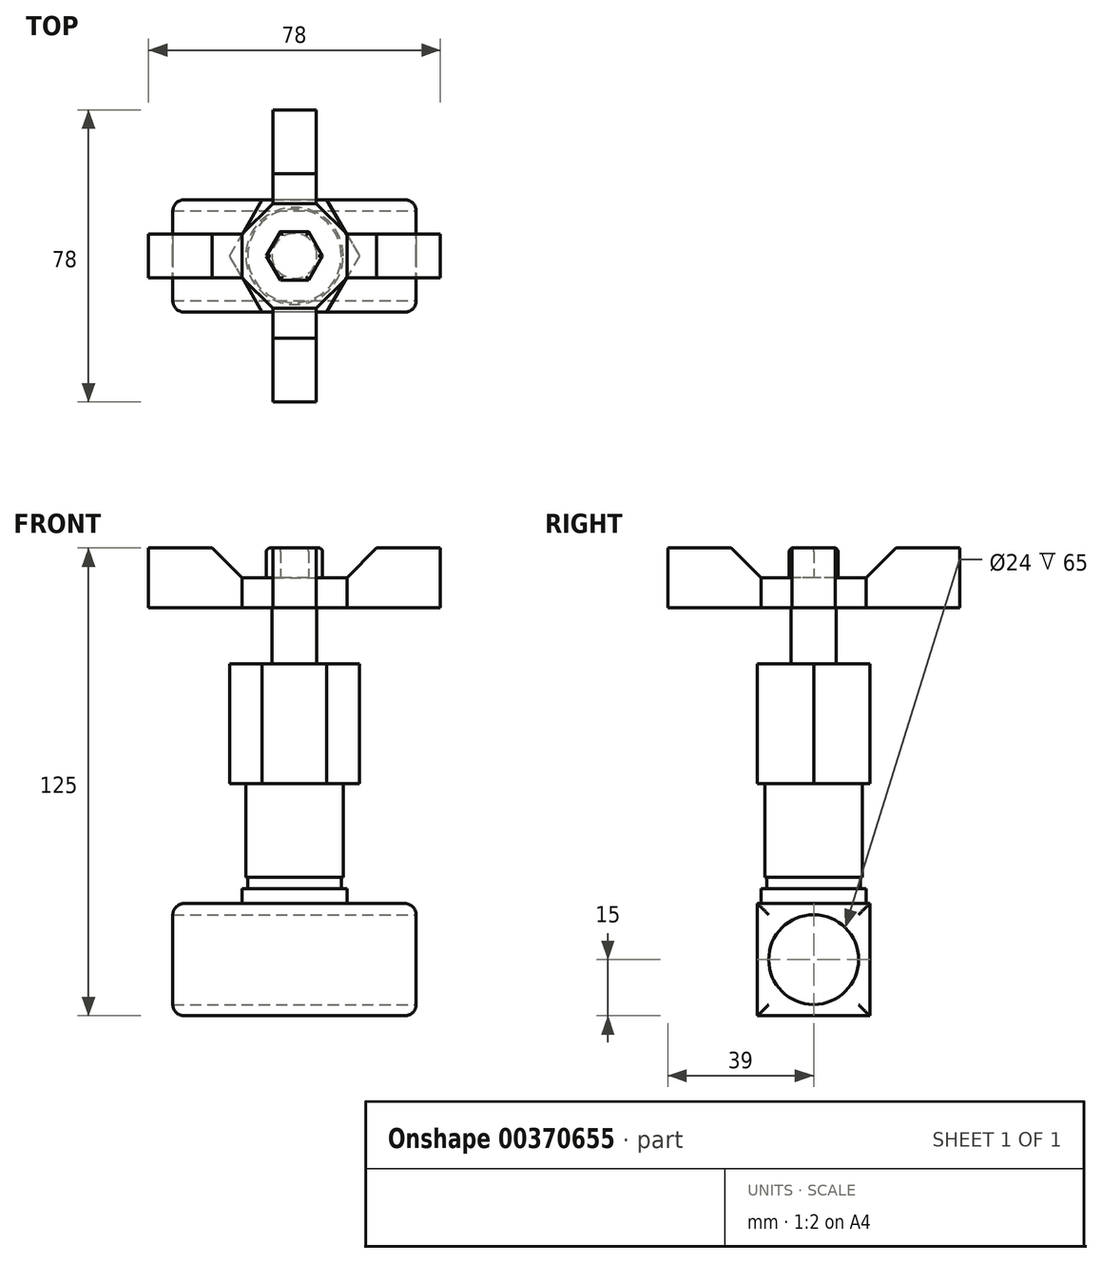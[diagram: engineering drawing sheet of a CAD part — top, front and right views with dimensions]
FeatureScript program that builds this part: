
annotation { "Feature Type Name" : "Feature", "Feature Type Description" : "" }
export const myFeature = defineFeature(function(context is Context, id is Id, definition is map)
    precondition{}
    {
        {
            var Q0;
            Q0=qCreatedBy(makeId("Top.planeOp"),FACE);
            var sketch = newSketch(context, id + "F0", { "sketchPlane" : qUnion([Q0])});
            skLineSegment(sketch, "E0.bottom", {"start": v(32.5, 15) * mm, "end": v(-32.5, 15) * mm});
            skLineSegment(sketch, "E0.top", {"start": v(32.5, -15) * mm, "end": v(-32.5, -15) * mm});
            skLineSegment(sketch, "E0.left", {"start": v(32.5, 15) * mm, "end": v(32.5, -15) * mm});
            skLineSegment(sketch, "E0.right", {"start": v(-32.5, 15) * mm, "end": v(-32.5, -15) * mm});
            skPoint(sketch, "E0.middle", {"position": v(0, 0) * mm});
            skSolve(sketch);
        }
        {
            var Q0;
            Q0=makeQuery(id+"F0.imprint","IMPRINT",FACE,{"disambiguationData":[TD([[makeQuery(id+"F0.imprint","IMPRINT",EDGE,{"derivedFrom":sQuery(id+"F0.wireOp",EDGE,"E0.bottom")}),1.0]])]});
            extrude(context, id + "F1", {"entities" : qUnion([Q0]), "depth" : 30 * mm});
        }
        {
            var Q0;
            Q0=makeQuery(id+"F1.opExtrude","SWEPT_FACE",FACE,{"disambiguationData":[OSD([sQuery(id+"F0.wireOp",EDGE,"E0.left")])]});
            var sketch = newSketch(context, id + "F2", { "sketchPlane" : qUnion([Q0])});
            skCircle(sketch, "E1", {"center": v(0, 15) * mm, "radius": 12 * mm});
            skSolve(sketch);
        }
        {
            var Q0;
            Q0=makeQuery(id+"F2.imprint","IMPRINT",FACE,{"disambiguationData":[TD([[makeQuery(id+"F2.imprint","IMPRINT",EDGE,{"derivedFrom":sQuery(id+"F2.wireOp",EDGE,"E1")}),1.0]])]});
            extrude(context, id + "F3", {"entities" : qUnion([Q0]), "operationType" : NewBodyOperationType.REMOVE, "oppositeDirection" : true, "depth" : 65 * mm});
        }
        {
            var Q0;
            Q0=makeQuery(id+"F1.opExtrude","CAP_FACE",FACE,{"disambiguationData":[OSD([sQuery(id+"F0.wireOp",EDGE,"E0.bottom"),sQuery(id+"F0.wireOp",EDGE,"E0.top"),sQuery(id+"F0.wireOp",EDGE,"E0.left"),sQuery(id+"F0.wireOp",EDGE,"E0.right")])],"isStart":false});
            var sketch = newSketch(context, id + "F4", { "sketchPlane" : qUnion([Q0])});
            skCircle(sketch, "E2", {"center": v(0, 0) * mm, "radius": 14 * mm});
            skSolve(sketch);
        }
        {
            var Q0;
            Q0=makeQuery(id+"F4.imprint","IMPRINT",FACE,{"disambiguationData":[TD([[makeQuery(id+"F4.imprint","IMPRINT",EDGE,{"derivedFrom":sQuery(id+"F4.wireOp",EDGE,"E2")}),1.0]])]});
            extrude(context, id + "F5", {"entities" : qUnion([Q0]), "operationType" : NewBodyOperationType.ADD, "depth" : 4 * mm});
        }
        {
            var Q0;
            Q0=makeQuery(id+"F5.opExtrude","CAP_FACE",FACE,{"disambiguationData":[OSD([sQuery(id+"F4.wireOp",EDGE,"E2")])],"isStart":false});
            var sketch = newSketch(context, id + "F6", { "sketchPlane" : qUnion([Q0])});
            skCircle(sketch, "E3", {"center": v(0, 0) * mm, "radius": 12.5 * mm});
            skSolve(sketch);
        }
        {
            var Q0;
            Q0=makeQuery(id+"F6.imprint","IMPRINT",FACE,{"disambiguationData":[TD([[makeQuery(id+"F6.imprint","IMPRINT",EDGE,{"derivedFrom":sQuery(id+"F6.wireOp",EDGE,"E3")}),1.0]])]});
            extrude(context, id + "F7", {"entities" : qUnion([Q0]), "operationType" : NewBodyOperationType.ADD, "depth" : 3 * mm});
        }
        {
            var Q0;
            Q0=makeQuery(id+"F7.opExtrude","CAP_FACE",FACE,{"disambiguationData":[OSD([sQuery(id+"F6.wireOp",EDGE,"E3")])],"isStart":false});
            var sketch = newSketch(context, id + "F8", { "sketchPlane" : qUnion([Q0])});
            skCircle(sketch, "E4", {"center": v(0, 0) * mm, "radius": 13 * mm});
            skSolve(sketch);
        }
        {
            var Q0;
            Q0=makeQuery(id+"F8.imprint","IMPRINT",FACE,{"disambiguationData":[TD([[makeQuery(id+"F8.imprint","IMPRINT",EDGE,{"derivedFrom":sQuery(id+"F8.wireOp",EDGE,"E4")}),1.0]])]});
            var Q1;
            Q1=makeQuery(id+"F8.imprint","IMPRINT",FACE,{"disambiguationData":[TD([[makeQuery(id+"F8.imprint","IMPRINT",EDGE,{"derivedFrom":makeQuery(id+"F7.opExtrude","CAP_EDGE",EDGE,{"disambiguationData":[OSD([sQuery(id+"F6.wireOp",EDGE,"E3")])],"isStart":false})}),1.0]])]});
            extrude(context, id + "F9", {"entities" : qUnion([Q0, Q1]), "operationType" : NewBodyOperationType.ADD, "depth" : 25 * mm});
        }
        {
            var Q0;
            Q0=makeQuery(id+"F9.opExtrude","CAP_FACE",FACE,{"disambiguationData":[OSD([sQuery(id+"F8.wireOp",EDGE,"E4")])],"isStart":false});
            var sketch = newSketch(context, id + "F10", { "sketchPlane" : qUnion([Q0])});
            skCircle(sketch, "E5.cCircle", {"center": v(0, 0) * mm, "radius": 15 * mm, "construction": true});
            skLineSegment(sketch, "E5.0", {"start": v(8.66, 15) * mm, "end": v(17.32, 0) * mm});
            skLineSegment(sketch, "E5.1", {"start": v(17.32, 0) * mm, "end": v(8.66, -15) * mm});
            skLineSegment(sketch, "E5.2", {"start": v(8.66, -15) * mm, "end": v(-8.66, -15) * mm});
            skLineSegment(sketch, "E5.3", {"start": v(-8.66, -15) * mm, "end": v(-17.32, 0) * mm});
            skLineSegment(sketch, "E5.4", {"start": v(-17.32, 0) * mm, "end": v(-8.66, 15) * mm});
            skLineSegment(sketch, "E5.5", {"start": v(-8.66, 15) * mm, "end": v(8.66, 15) * mm});
            skPoint(sketch, "E5.0.midPoint", {"position": v(13, 7.5) * mm});
            skSolve(sketch);
        }
        {
            var Q0;
            Q0=makeQuery(id+"F10.imprint","IMPRINT",FACE,{"disambiguationData":[TD([[makeQuery(id+"F10.imprint","IMPRINT",EDGE,{"derivedFrom":makeQuery(id+"F9.opExtrude","CAP_EDGE",EDGE,{"disambiguationData":[OSD([sQuery(id+"F8.wireOp",EDGE,"E4")])],"isStart":false})}),1.0]])]});
            var Q1;
            Q1=makeQuery(id+"F10.imprint","IMPRINT",FACE,{"disambiguationData":[TD([[makeQuery(id+"F10.imprint","IMPRINT",EDGE,{"derivedFrom":sQuery(id+"F10.wireOp",EDGE,"E5.0")}),-1.0]])]});
            extrude(context, id + "F11", {"entities" : qUnion([Q0, Q1]), "operationType" : NewBodyOperationType.ADD, "depth" : 32 * mm});
        }
        {
            var Q0;
            Q0=makeQuery(id+"F11.opExtrude","CAP_FACE",FACE,{"disambiguationData":[OSD([sQuery(id+"F10.wireOp",EDGE,"E5.0"),sQuery(id+"F10.wireOp",EDGE,"E5.1"),sQuery(id+"F10.wireOp",EDGE,"E5.2"),sQuery(id+"F10.wireOp",EDGE,"E5.3"),sQuery(id+"F10.wireOp",EDGE,"E5.4"),sQuery(id+"F10.wireOp",EDGE,"E5.5")])],"isStart":false});
            var sketch = newSketch(context, id + "F12", { "sketchPlane" : qUnion([Q0])});
            skCircle(sketch, "E6", {"center": v(0, 0) * mm, "radius": 6 * mm});
            skSolve(sketch);
        }
        {
            var Q0;
            Q0=makeQuery(id+"F12.imprint","IMPRINT",FACE,{"disambiguationData":[TD([[makeQuery(id+"F12.imprint","IMPRINT",EDGE,{"derivedFrom":sQuery(id+"F12.wireOp",EDGE,"E6")}),1.0]])]});
            extrude(context, id + "F13", {"entities" : qUnion([Q0]), "operationType" : NewBodyOperationType.ADD, "depth" : 15 * mm});
        }
        {
            var Q0;
            Q0=makeQuery(id+"F13.opExtrude","CAP_FACE",FACE,{"disambiguationData":[OSD([sQuery(id+"F12.wireOp",EDGE,"E6")])],"isStart":false});
            var sketch = newSketch(context, id + "F14", { "sketchPlane" : qUnion([Q0])});
            skCircle(sketch, "E7.cCircle", {"center": v(0, 0) * mm, "radius": 14 * mm, "construction": true});
            skLineSegment(sketch, "E7.0", {"start": v(14, -5.8) * mm, "end": v(5.8, -14) * mm});
            skLineSegment(sketch, "E7.1", {"start": v(5.8, -14) * mm, "end": v(-5.8, -14) * mm});
            skLineSegment(sketch, "E7.2", {"start": v(-5.8, -14) * mm, "end": v(-14, -5.8) * mm});
            skLineSegment(sketch, "E7.3", {"start": v(-14, -5.8) * mm, "end": v(-14, 5.8) * mm});
            skLineSegment(sketch, "E7.4", {"start": v(-14, 5.8) * mm, "end": v(-5.8, 14) * mm});
            skLineSegment(sketch, "E7.5", {"start": v(-5.8, 14) * mm, "end": v(5.8, 14) * mm});
            skLineSegment(sketch, "E7.6", {"start": v(5.8, 14) * mm, "end": v(14, 5.8) * mm});
            skLineSegment(sketch, "E7.7", {"start": v(14, 5.8) * mm, "end": v(14, -5.8) * mm});
            skPoint(sketch, "E7.0.midPoint", {"position": v(9.9, -9.9) * mm});
            skSolve(sketch);
        }
        {
            var Q0;
            Q0=makeQuery(id+"F14.imprint","IMPRINT",FACE,{"disambiguationData":[TD([[makeQuery(id+"F14.imprint","IMPRINT",EDGE,{"derivedFrom":makeQuery(id+"F13.opExtrude","CAP_EDGE",EDGE,{"disambiguationData":[OSD([sQuery(id+"F12.wireOp",EDGE,"E6")])],"isStart":false})}),1.0]])]});
            var Q1;
            Q1=makeQuery(id+"F14.imprint","IMPRINT",FACE,{"disambiguationData":[TD([[makeQuery(id+"F14.imprint","IMPRINT",EDGE,{"derivedFrom":sQuery(id+"F14.wireOp",EDGE,"E7.0")}),-1.0]])]});
            extrude(context, id + "F15", {"entities" : qUnion([Q0, Q1]), "operationType" : NewBodyOperationType.ADD, "depth" : 8 * mm});
        }
        {
            var Q0;
            Q0=makeQuery(id+"F15.opExtrude","SWEPT_FACE",FACE,{"disambiguationData":[OSD([sQuery(id+"F14.wireOp",EDGE,"E7.7")])]});
            extrude(context, id + "F16", {"entities" : qUnion([Q0]), "operationType" : NewBodyOperationType.ADD, "depth" : 25 * mm});
        }
        {
            var Q0;
            Q0=makeQuery(id+"F15.opExtrude","SWEPT_FACE",FACE,{"disambiguationData":[OSD([sQuery(id+"F14.wireOp",EDGE,"E7.1")])]});
            extrude(context, id + "F17", {"entities" : qUnion([Q0]), "operationType" : NewBodyOperationType.ADD, "depth" : 25 * mm});
        }
        {
            var Q0;
            Q0=makeQuery(id+"F15.opExtrude","SWEPT_FACE",FACE,{"disambiguationData":[OSD([sQuery(id+"F14.wireOp",EDGE,"E7.3")])]});
            extrude(context, id + "F18", {"entities" : qUnion([Q0]), "operationType" : NewBodyOperationType.ADD, "depth" : 25 * mm});
        }
        {
            var Q0;
            Q0=makeQuery(id+"F15.opExtrude","SWEPT_FACE",FACE,{"disambiguationData":[OSD([sQuery(id+"F14.wireOp",EDGE,"E7.5")])]});
            extrude(context, id + "F19", {"entities" : qUnion([Q0]), "operationType" : NewBodyOperationType.ADD, "depth" : 25 * mm});
        }
        {
            var Q0;
            {var subQ0=sQuery(id+"F14.wireOp",EDGE,"E7.5");var subQ1=sQuery(id+"F14.wireOp",EDGE,"E7.3");var subQ2=sQuery(id+"F14.wireOp",EDGE,"E7.1");var subQ3=sQuery(id+"F14.wireOp",EDGE,"E7.7");Q0=makeQuery(id+"F19.boolean.opBoolean","MERGE",FACE,{"derivedFrom":[makeQuery(id+"F18.boolean.opBoolean","MERGE",FACE,{"derivedFrom":[makeQuery(id+"F17.boolean.opBoolean","MERGE",FACE,{"derivedFrom":[makeQuery(id+"F16.boolean.opBoolean","MERGE",FACE,{"derivedFrom":[makeQuery(id+"F15.opExtrude","CAP_FACE",FACE,{"disambiguationData":[OSD([sQuery(id+"F14.wireOp",EDGE,"E7.0"),subQ2,sQuery(id+"F14.wireOp",EDGE,"E7.2"),subQ1,sQuery(id+"F14.wireOp",EDGE,"E7.4"),subQ0,sQuery(id+"F14.wireOp",EDGE,"E7.6"),subQ3])],"isStart":false}),makeQuery(id+"F16.opExtrude","SWEPT_FACE",FACE,{"disambiguationData":[OSD([subQ3]),TDD([makeQuery(id+"F15.opExtrude","CAP_EDGE",EDGE,{"disambiguationData":[OSD([subQ3])],"isStart":false})])]})]}),makeQuery(id+"F17.opExtrude","SWEPT_FACE",FACE,{"disambiguationData":[OSD([subQ2]),TDD([makeQuery(id+"F15.opExtrude","CAP_EDGE",EDGE,{"disambiguationData":[OSD([subQ2])],"isStart":false})])]})]}),makeQuery(id+"F18.opExtrude","SWEPT_FACE",FACE,{"disambiguationData":[OSD([subQ1]),TDD([makeQuery(id+"F15.opExtrude","CAP_EDGE",EDGE,{"disambiguationData":[OSD([subQ1])],"isStart":false})])]})]}),makeQuery(id+"F19.opExtrude","SWEPT_FACE",FACE,{"disambiguationData":[OSD([subQ0]),TDD([makeQuery(id+"F15.opExtrude","CAP_EDGE",EDGE,{"disambiguationData":[OSD([subQ0])],"isStart":false})])]})]});}
            var sketch = newSketch(context, id + "F20", { "sketchPlane" : qUnion([Q0])});
            skLineSegment(sketch, "E8.bottom", {"start": v(39, 5.8) * mm, "end": v(14, 5.8) * mm});
            skLineSegment(sketch, "E8.top", {"start": v(39, -5.8) * mm, "end": v(14, -5.8) * mm});
            skLineSegment(sketch, "E8.left", {"start": v(39, 5.8) * mm, "end": v(39, -5.8) * mm});
            skLineSegment(sketch, "E8.right", {"start": v(14, 5.8) * mm, "end": v(14, -5.8) * mm});
            skLineSegment(sketch, "E9.bottom", {"start": v(-5.8, 39) * mm, "end": v(5.8, 39) * mm});
            skLineSegment(sketch, "E9.top", {"start": v(-5.8, 14) * mm, "end": v(5.8, 14) * mm});
            skLineSegment(sketch, "E9.left", {"start": v(-5.8, 39) * mm, "end": v(-5.8, 14) * mm});
            skLineSegment(sketch, "E9.right", {"start": v(5.8, 39) * mm, "end": v(5.8, 14) * mm});
            skLineSegment(sketch, "E10.bottom", {"start": v(-39, -5.8) * mm, "end": v(-14, -5.8) * mm});
            skLineSegment(sketch, "E10.top", {"start": v(-39, 5.8) * mm, "end": v(-14, 5.8) * mm});
            skLineSegment(sketch, "E10.left", {"start": v(-39, -5.8) * mm, "end": v(-39, 5.8) * mm});
            skLineSegment(sketch, "E10.right", {"start": v(-14, -5.8) * mm, "end": v(-14, 5.8) * mm});
            skLineSegment(sketch, "E11.bottom", {"start": v(-5.8, -39) * mm, "end": v(5.8, -39) * mm});
            skLineSegment(sketch, "E11.top", {"start": v(-5.8, -14) * mm, "end": v(5.8, -14) * mm});
            skLineSegment(sketch, "E11.left", {"start": v(-5.8, -39) * mm, "end": v(-5.8, -14) * mm});
            skLineSegment(sketch, "E11.right", {"start": v(5.8, -39) * mm, "end": v(5.8, -14) * mm});
            skSolve(sketch);
        }
        {
            var Q0;
            {var subQ0=sQuery(id+"F20.wireOp",EDGE,"E9.top");Q0=makeQuery(id+"F20.imprint","IMPRINT",FACE,{"disambiguationData":[TD([[makeQuery(id+"F20.imprint","IMPRINT",EDGE,{"derivedFrom":subQ0}),1.0]])]});}
            var Q1;
            {var subQ0=sQuery(id+"F20.wireOp",EDGE,"E10.bottom");Q1=makeQuery(id+"F20.imprint","IMPRINT",FACE,{"disambiguationData":[TD([[makeQuery(id+"F20.imprint","IMPRINT",EDGE,{"derivedFrom":subQ0}),1.0]])]});}
            var Q2;
            {var subQ1=sQuery(id+"F14.wireOp",EDGE,"E7.1");var subQ2=sQuery(id+"F14.wireOp",EDGE,"E7.2");var subQ3=makeQuery(id+"F17.opExtrude","SWEPT_EDGE",EDGE,{"disambiguationData":[OSD([subQ1,subQ2]),TDD([makeQuery(id+"F15.opExtrude","CAP_VERTEX",VERTEX,{"disambiguationData":[OSD([subQ1,subQ2])],"isStart":false})])]});var subQ8=sQuery(id+"F20.wireOp",EDGE,"E11.top");var subQ10=makeQuery(id+"F20.imprint","INTERSECT",VERTEX,{"derivedFrom":[subQ3,subQ8]});Q2=makeQuery(id+"F20.imprint","IMPRINT",FACE,{"disambiguationData":[TD([[makeQuery(id+"F20.imprint","IMPRINT",EDGE,{"disambiguationData":[TD([[subQ10,-1.0]])],"derivedFrom":subQ8}),-1.0]])]});}
            var Q3;
            {var subQ0=sQuery(id+"F20.wireOp",EDGE,"E8.bottom");Q3=makeQuery(id+"F20.imprint","IMPRINT",FACE,{"disambiguationData":[TD([[makeQuery(id+"F20.imprint","IMPRINT",EDGE,{"derivedFrom":subQ0}),1.0]])]});}
            extrude(context, id + "F21", {"entities" : qUnion([Q0, Q1, Q2, Q3]), "operationType" : NewBodyOperationType.ADD, "depth" : 8 * mm});
        }
        {
            var Q0;
            Q0=makeQuery(id+"F21.opExtrude","CAP_EDGE",EDGE,{"disambiguationData":[OSD([sQuery(id+"F20.wireOp",EDGE,"E10.right")])],"isStart":false});
            var Q1;
            Q1=makeQuery(id+"F21.opExtrude","CAP_EDGE",EDGE,{"disambiguationData":[OSD([sQuery(id+"F20.wireOp",EDGE,"E11.top")])],"isStart":false});
            var Q2;
            Q2=makeQuery(id+"F21.opExtrude","CAP_EDGE",EDGE,{"disambiguationData":[OSD([sQuery(id+"F20.wireOp",EDGE,"E8.right")])],"isStart":false});
            var Q3;
            Q3=makeQuery(id+"F21.opExtrude","CAP_EDGE",EDGE,{"disambiguationData":[OSD([sQuery(id+"F20.wireOp",EDGE,"E9.top")])],"isStart":false});
            chamfer(context, id + "F22", {"entities" : qUnion([Q0, Q1, Q2, Q3]), "width" : 8 * mm, "tangentPropagation" : true});
        }
        {
            var Q0;
            Q0=makeQuery(id+"F1.opExtrude","SWEPT_EDGE",EDGE,{"disambiguationData":[OSD([sQuery(id+"F0.wireOp",EDGE,"E0.top"),sQuery(id+"F0.wireOp",EDGE,"E0.left")])]});
            var Q1;
            Q1=makeQuery(id+"F1.opExtrude","CAP_EDGE",EDGE,{"disambiguationData":[OSD([sQuery(id+"F0.wireOp",EDGE,"E0.left")])],"isStart":false});
            var Q2;
            Q2=makeQuery(id+"F1.opExtrude","SWEPT_EDGE",EDGE,{"disambiguationData":[OSD([sQuery(id+"F0.wireOp",EDGE,"E0.bottom"),sQuery(id+"F0.wireOp",EDGE,"E0.left")])]});
            var Q3;
            Q3=makeQuery(id+"F1.opExtrude","CAP_EDGE",EDGE,{"disambiguationData":[OSD([sQuery(id+"F0.wireOp",EDGE,"E0.left")])],"isStart":true});
            fillet(context, id + "F23", {"entities" : qUnion([Q0, Q1, Q2, Q3]), "radius" : 3 * mm, "tangentPropagation" : true, "allowEdgeOverflow" : false});
        }
        {
            var Q0;
            Q0=makeQuery(id+"F1.opExtrude","CAP_EDGE",EDGE,{"disambiguationData":[OSD([sQuery(id+"F0.wireOp",EDGE,"E0.right")])],"isStart":false});
            var Q1;
            Q1=makeQuery(id+"F1.opExtrude","SWEPT_EDGE",EDGE,{"disambiguationData":[OSD([sQuery(id+"F0.wireOp",EDGE,"E0.bottom"),sQuery(id+"F0.wireOp",EDGE,"E0.right")])]});
            var Q2;
            Q2=makeQuery(id+"F1.opExtrude","SWEPT_EDGE",EDGE,{"disambiguationData":[OSD([sQuery(id+"F0.wireOp",EDGE,"E0.top"),sQuery(id+"F0.wireOp",EDGE,"E0.right")])]});
            var Q3;
            Q3=makeQuery(id+"F1.opExtrude","CAP_EDGE",EDGE,{"disambiguationData":[OSD([sQuery(id+"F0.wireOp",EDGE,"E0.right")])],"isStart":true});
            fillet(context, id + "F24", {"entities" : qUnion([Q0, Q1, Q2, Q3]), "radius" : 3 * mm, "tangentPropagation" : true, "allowEdgeOverflow" : false});
        }
        {
            var Q0;
            {var subQ0=sQuery(id+"F14.wireOp",EDGE,"E7.5");var subQ1=sQuery(id+"F14.wireOp",EDGE,"E7.4");var subQ2=sQuery(id+"F14.wireOp",EDGE,"E7.3");var subQ3=makeQuery(id+"F18.opExtrude","SWEPT_FACE",FACE,{"disambiguationData":[OSD([subQ2]),TDD([makeQuery(id+"F15.opExtrude","CAP_EDGE",EDGE,{"disambiguationData":[OSD([subQ2])],"isStart":false})])]});var subQ4=sQuery(id+"F14.wireOp",EDGE,"E7.1");var subQ5=makeQuery(id+"F17.opExtrude","SWEPT_FACE",FACE,{"disambiguationData":[OSD([subQ4]),TDD([makeQuery(id+"F15.opExtrude","CAP_EDGE",EDGE,{"disambiguationData":[OSD([subQ4])],"isStart":false})])]});var subQ6=sQuery(id+"F14.wireOp",EDGE,"E7.2");var subQ7=makeQuery(id+"F19.opExtrude","SWEPT_FACE",FACE,{"disambiguationData":[OSD([subQ0]),TDD([makeQuery(id+"F15.opExtrude","CAP_EDGE",EDGE,{"disambiguationData":[OSD([subQ0])],"isStart":false})])]});var subQ8=sQuery(id+"F14.wireOp",EDGE,"E7.7");var subQ9=makeQuery(id+"F16.opExtrude","SWEPT_FACE",FACE,{"disambiguationData":[OSD([subQ8]),TDD([makeQuery(id+"F15.opExtrude","CAP_EDGE",EDGE,{"disambiguationData":[OSD([subQ8])],"isStart":false})])]});var subQ10=sQuery(id+"F14.wireOp",EDGE,"E7.0");var subQ11=sQuery(id+"F14.wireOp",EDGE,"E7.6");var subQ12=makeQuery(id+"F15.opExtrude","CAP_FACE",FACE,{"disambiguationData":[OSD([subQ10,subQ4,subQ6,subQ2,subQ1,subQ0,subQ11,subQ8])],"isStart":false});Q0=makeQuery(id+"F21.boolean.opBoolean","SPLIT",FACE,{"disambiguationData":[TD([makeQuery(id+"F15.opExtrude","SWEPT_FACE",FACE,{"disambiguationData":[OSD([subQ10])]}),subQ12,makeQuery(id+"F15.opExtrude","SWEPT_FACE",FACE,{"disambiguationData":[OSD([subQ6])]}),makeQuery(id+"F15.opExtrude","SWEPT_FACE",FACE,{"disambiguationData":[OSD([subQ1])]}),makeQuery(id+"F15.opExtrude","SWEPT_FACE",FACE,{"disambiguationData":[OSD([subQ11])]}),makeQuery(id+"F16.opExtrude","SWEPT_FACE",FACE,{"disambiguationData":[OSD([subQ10,subQ8])]}),makeQuery(id+"F16.opExtrude","SWEPT_FACE",FACE,{"disambiguationData":[OSD([subQ11,subQ8])]}),subQ9,makeQuery(id+"F16.opExtrude","CAP_FACE",FACE,{"disambiguationData":[OSD([subQ8])],"isStart":false}),makeQuery(id+"F17.opExtrude","SWEPT_FACE",FACE,{"disambiguationData":[OSD([subQ10,subQ4])]}),makeQuery(id+"F17.opExtrude","SWEPT_FACE",FACE,{"disambiguationData":[OSD([subQ4,subQ6])]}),subQ5,makeQuery(id+"F18.opExtrude","SWEPT_FACE",FACE,{"disambiguationData":[OSD([subQ6,subQ2])]}),makeQuery(id+"F18.opExtrude","SWEPT_FACE",FACE,{"disambiguationData":[OSD([subQ2,subQ1])]}),subQ3,makeQuery(id+"F18.opExtrude","CAP_FACE",FACE,{"disambiguationData":[OSD([subQ2])],"isStart":false}),makeQuery(id+"F19.opExtrude","SWEPT_FACE",FACE,{"disambiguationData":[OSD([subQ1,subQ0])]}),makeQuery(id+"F19.opExtrude","SWEPT_FACE",FACE,{"disambiguationData":[OSD([subQ0,subQ11])]}),subQ7,makeQuery(id+"F19.opExtrude","CAP_FACE",FACE,{"disambiguationData":[OSD([subQ0])],"isStart":false}),makeQuery(id+"F21.opExtrude","SWEPT_FACE",FACE,{"disambiguationData":[OSD([sQuery(id+"F20.wireOp",EDGE,"E8.bottom")])]}),makeQuery(id+"F21.opExtrude","SWEPT_FACE",FACE,{"disambiguationData":[OSD([sQuery(id+"F20.wireOp",EDGE,"E8.top")])]}),makeQuery(id+"F21.opExtrude","SWEPT_FACE",FACE,{"disambiguationData":[OSD([sQuery(id+"F20.wireOp",EDGE,"E8.right")])]}),makeQuery(id+"F21.opExtrude","SWEPT_FACE",FACE,{"disambiguationData":[OSD([sQuery(id+"F20.wireOp",EDGE,"E9.top")])]}),makeQuery(id+"F21.opExtrude","SWEPT_FACE",FACE,{"disambiguationData":[OSD([sQuery(id+"F20.wireOp",EDGE,"E9.left")])]}),makeQuery(id+"F21.opExtrude","SWEPT_FACE",FACE,{"disambiguationData":[OSD([sQuery(id+"F20.wireOp",EDGE,"E9.right")])]}),makeQuery(id+"F21.opExtrude","SWEPT_FACE",FACE,{"disambiguationData":[OSD([sQuery(id+"F20.wireOp",EDGE,"E10.bottom")])]}),makeQuery(id+"F21.opExtrude","SWEPT_FACE",FACE,{"disambiguationData":[OSD([sQuery(id+"F20.wireOp",EDGE,"E10.top")])]}),makeQuery(id+"F21.opExtrude","SWEPT_FACE",FACE,{"disambiguationData":[OSD([sQuery(id+"F20.wireOp",EDGE,"E10.right")])]}),makeQuery(id+"F21.opExtrude","SWEPT_FACE",FACE,{"disambiguationData":[OSD([sQuery(id+"F20.wireOp",EDGE,"E11.top")])]}),makeQuery(id+"F21.opExtrude","SWEPT_FACE",FACE,{"disambiguationData":[OSD([subQ8])]}),makeQuery(id+"F21.opExtrude","SWEPT_FACE",FACE,{"disambiguationData":[OSD([subQ10,subQ4])]}),makeQuery(id+"F21.opExtrude","SWEPT_FACE",FACE,{"disambiguationData":[OSD([subQ4,subQ6])]}),makeQuery(id+"F21.opExtrude","SWEPT_FACE",FACE,{"disambiguationData":[OSD([subQ2])]}),makeQuery(id+"F21.opExtrude","SWEPT_FACE",FACE,{"disambiguationData":[OSD([subQ0])]})])],"derivedFrom":makeQuery(id+"F19.boolean.opBoolean","MERGE",FACE,{"derivedFrom":[makeQuery(id+"F18.boolean.opBoolean","MERGE",FACE,{"derivedFrom":[makeQuery(id+"F17.boolean.opBoolean","MERGE",FACE,{"derivedFrom":[makeQuery(id+"F16.boolean.opBoolean","MERGE",FACE,{"derivedFrom":[subQ12,subQ9]}),subQ5]}),subQ3]}),subQ7]})});}
            var sketch = newSketch(context, id + "F25", { "sketchPlane" : qUnion([Q0])});
            skCircle(sketch, "E12.cCircle", {"center": v(0, 0) * mm, "radius": 6.5 * mm, "construction": true});
            skLineSegment(sketch, "E12.0", {"start": v(3.75, 6.5) * mm, "end": v(7.5, 0) * mm});
            skLineSegment(sketch, "E12.1", {"start": v(7.5, 0) * mm, "end": v(3.75, -6.5) * mm});
            skLineSegment(sketch, "E12.2", {"start": v(3.75, -6.5) * mm, "end": v(-3.75, -6.5) * mm});
            skLineSegment(sketch, "E12.3", {"start": v(-3.75, -6.5) * mm, "end": v(-7.5, 0) * mm});
            skLineSegment(sketch, "E12.4", {"start": v(-7.5, 0) * mm, "end": v(-3.75, 6.5) * mm});
            skLineSegment(sketch, "E12.5", {"start": v(-3.75, 6.5) * mm, "end": v(3.75, 6.5) * mm});
            skPoint(sketch, "E12.0.midPoint", {"position": v(5.63, 3.25) * mm});
            skSolve(sketch);
        }
        {
            var Q0;
            Q0=makeQuery(id+"F25.imprint","IMPRINT",FACE,{"disambiguationData":[TD([[makeQuery(id+"F25.imprint","IMPRINT",EDGE,{"derivedFrom":sQuery(id+"F25.wireOp",EDGE,"E12.0")}),-1.0]])]});
            extrude(context, id + "F26", {"entities" : qUnion([Q0]), "operationType" : NewBodyOperationType.ADD, "depth" : 8 * mm});
        }
        {
            var Q0;
            Q0=makeQuery(id+"F26.opExtrude","CAP_EDGE",EDGE,{"disambiguationData":[OSD([sQuery(id+"F25.wireOp",EDGE,"E12.2")])],"isStart":false});
            var Q1;
            Q1=makeQuery(id+"F26.opExtrude","CAP_EDGE",EDGE,{"disambiguationData":[OSD([sQuery(id+"F25.wireOp",EDGE,"E12.3")])],"isStart":false});
            var Q2;
            Q2=makeQuery(id+"F26.opExtrude","CAP_EDGE",EDGE,{"disambiguationData":[OSD([sQuery(id+"F25.wireOp",EDGE,"E12.4")])],"isStart":false});
            var Q3;
            Q3=makeQuery(id+"F26.opExtrude","CAP_EDGE",EDGE,{"disambiguationData":[OSD([sQuery(id+"F25.wireOp",EDGE,"E12.5")])],"isStart":false});
            var Q4;
            Q4=makeQuery(id+"F26.opExtrude","CAP_EDGE",EDGE,{"disambiguationData":[OSD([sQuery(id+"F25.wireOp",EDGE,"E12.0")])],"isStart":false});
            var Q5;
            Q5=makeQuery(id+"F26.opExtrude","CAP_EDGE",EDGE,{"disambiguationData":[OSD([sQuery(id+"F25.wireOp",EDGE,"E12.1")])],"isStart":false});
            fillet(context, id + "F27", {"entities" : qUnion([Q0, Q1, Q2, Q3, Q4, Q5]), "radius" : 1 * mm, "tangentPropagation" : true, "allowEdgeOverflow" : false});
        }
    });
